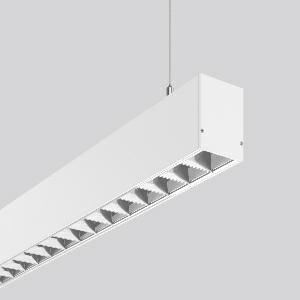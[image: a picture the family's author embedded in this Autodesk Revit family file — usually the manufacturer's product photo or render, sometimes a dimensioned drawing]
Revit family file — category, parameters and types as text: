
# Revit family: less_is_more_50_312337_002_1_44e0
name_source: partatom
category: Lighting Fixtures
units: mm (PartAtom-declared; Revit-internal decimal feet)

## family parameters
Cut with Voids When Loaded = No
Host = Face
Light Source = No
Part Type = Normal
Room Calculation Point = No
Round Connector Dimension = Use Diameter
Shared = No

## types (1)
- LESS IS MORE 50 (1 x LED Modul 840, 4450 lm, 4000)
    Apparent Load = 35 VA
    CIE Flux Codes = 95 100 100 100 100
    Color Rendering = 80
    Color Temperature = 4000
    Default Elevation = 1800 mm
    Description = Series: LESS IS MORE 50
Linear pendant luminaire for aesthetically sophisticated lighting. Housing: extruded aluminium profile, powder-coated. End cap aluminium powder-coated. Canopy made of aluminium, powder-coated. Alea optical system: Reflector structure (ABS, Aluminium-coated, highly polished) with integrated diffuser made of non-yellowing plastic (PMMA) opal for glare-free light at the workstation (screen-compliant according to EN 12464-1). Direct light emission. Suitable for pendant. 2-point steel cable suspension freely positionable and infinitely height-adjustable. Special lengths available on request. LED unit with integrated converter interchangeable and removable. Suitable for through-wiring. With sensors or as a safety luminaire on request. 
Colour: traffic white, matt (RAL 9016)
Length: 1407 mm
Width: 57 mm
Height: 75 mm
Suspension length: 2000 mm
Lamp: LED
Socket: without socket
Colour temperature: 4000K
Colour rendering index (CRI): 80
System power: 35 W
Rated luminous flux: 4450 lm
Luminous efficiency: 127 lm/W
Control gear: Regulated power supply
Protection class: I
Type of protection: IP 20
    Height = 75 mm
    Lamp = 1 x LED Modul 840
    Lamp Light Flux = 4450 lm
    Lamp count = 1
    Length = 1407 mm
    Lifetime = 50000 h
    Luminous efficacy = 127 lm/W
    Manufacturer = RZB
    ModVariant = No
    Model = 312337.002.1
    Mounting Place = Ceiling
    Mounting Type = Pendant
    Number of Poles = 1
    OnlyDefault = Yes
    Power Factor = 1
    Product Name = LESS IS MORE 50
    Product group = Pendant LED linear luminaires
    ProductGroupID = 907
    Protection Class = Protection class I
    Protection Degree = IP 20
    RLX_Detail_Level = 1
    RLX_Emergency_Light_Flux = 0 lm
    RLX_Emergency_Type = 0
    RLX_Emergency_Type_DB = No
    RlxData = <blob elided: 33169 chars, md5=c1d4a08c>
    Socket = socket
    Standby Power = 0 W
    System Light Flux = 4450 lm
    System Power = 35 W
    Type Comments = Product without accessories
    Type Image = 312342.002.jpg
    URL = http://relux.com
    VarID = ---
    Voltage = 230 V
    Voltage Range = 220-240 V
    Weight = 0.00 kg
    Width = 57 mm

## geometry (parser evidence)
native form markers: Blend x4, Sweep x8
no freeform markers — native parametric forms only
